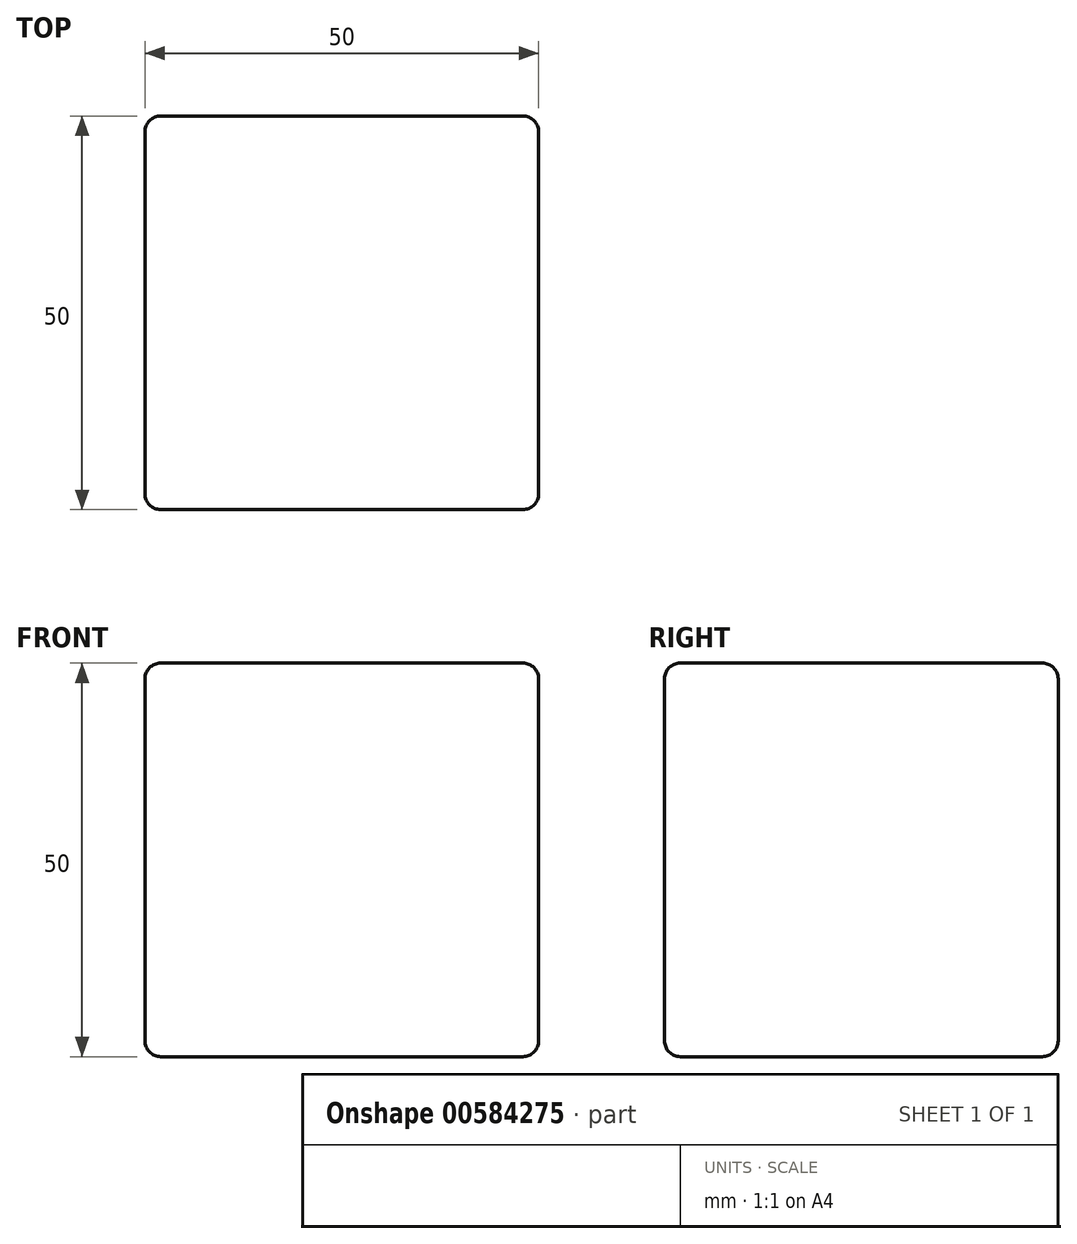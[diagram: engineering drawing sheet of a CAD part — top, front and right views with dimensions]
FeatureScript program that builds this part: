
annotation { "Feature Type Name" : "Feature", "Feature Type Description" : "" }
export const myFeature = defineFeature(function(context is Context, id is Id, definition is map)
    precondition{}
    {
        {
            var Q0;
            Q0=qCreatedBy(makeId("Top.planeOp"),FACE);
            var sketch = newSketch(context, id + "F0", { "sketchPlane" : qUnion([Q0])});
            skLineSegment(sketch, "E0.bottom", {"start": v(-25, 25) * mm, "end": v(25, 25) * mm});
            skLineSegment(sketch, "E0.top", {"start": v(-25, -25) * mm, "end": v(25, -25) * mm});
            skLineSegment(sketch, "E0.left", {"start": v(-25, 25) * mm, "end": v(-25, -25) * mm});
            skLineSegment(sketch, "E0.right", {"start": v(25, 25) * mm, "end": v(25, -25) * mm});
            skSolve(sketch);
        }
        {
            var Q0;
            Q0=makeQuery(id+"F0.imprint","IMPRINT",FACE,{"disambiguationData":[TD([[makeQuery(id+"F0.imprint","IMPRINT",EDGE,{"derivedFrom":sQuery(id+"F0.wireOp",EDGE,"E0.bottom")}),-1.0]])]});
            extrude(context, id + "F1", {"entities" : qUnion([Q0]), "depth" : 50 * mm, "offsetDistance" : 25 * mm});
        }
        {
            var Q0;
            Q0=makeQuery(id+"F1.opExtrude","CAP_FACE",FACE,{"disambiguationData":[OSD([sQuery(id+"F0.wireOp",EDGE,"E0.bottom"),sQuery(id+"F0.wireOp",EDGE,"E0.top"),sQuery(id+"F0.wireOp",EDGE,"E0.left"),sQuery(id+"F0.wireOp",EDGE,"E0.right")])],"isStart":false});
            var Q1;
            Q1=makeQuery(id+"F1.opExtrude","SWEPT_FACE",FACE,{"disambiguationData":[OSD([sQuery(id+"F0.wireOp",EDGE,"E0.left")])]});
            var Q2;
            Q2=makeQuery(id+"F1.opExtrude","SWEPT_FACE",FACE,{"disambiguationData":[OSD([sQuery(id+"F0.wireOp",EDGE,"E0.bottom")])]});
            var Q3;
            Q3=makeQuery(id+"F1.opExtrude","SWEPT_FACE",FACE,{"disambiguationData":[OSD([sQuery(id+"F0.wireOp",EDGE,"E0.right")])]});
            var Q4;
            Q4=makeQuery(id+"F1.opExtrude","SWEPT_FACE",FACE,{"disambiguationData":[OSD([sQuery(id+"F0.wireOp",EDGE,"E0.top")])]});
            fillet(context, id + "F2", {"entities" : qUnion([Q0, Q1, Q2, Q3, Q4]), "radius" : 2 * mm, "tangentPropagation" : true, "allowEdgeOverflow" : false});
        }
    });
